# Revit family: H3006-TR035-EB
name_source: partatom
category: Aparatos sanitarios
units: mm (PartAtom-declared; Revit-internal decimal feet)

## family parameters
Anfitrión = Cara
Compartido = Sí
Corte con vacíos al cargar = No
Cota de conector redondo = Diámetro de uso
Número OmniClass = 23.45.05.14.17
Punto de cálculo de habitación = Sí
Tipo de pieza = Normal
Título OmniClass = Showers

## types (3) — shared parameters
Conexión = ½"-14 NPSM
Elevación por defecto = 0.5 "
Fabricante = HELVEX S.A. DE C.V.
Imagen de tipo = <Ninguno>
Presión máxima de trabajo = 85.3 psi
Presión mínima de trabajo = 14.2 psi

## per-type parameters (varying)
| type | Comentarios de tipo | Descripción | Material | Material EC | Modelo | Total Diameter | Total Length | URL |
| H3005-TR035 | Regadera redonda de plato ancho, multichorro 10"
3 Chorros.
3 Chorros. | Regadera redonda de plato ancho, multichorro 10"
3 Chorros.
3 Chorros. | 192_192_192 | <Por categoría> | H3005-TR035-EB | 9.6 " | 22.2 " |  |
| H3005-TR035-EB | Regadera de media y alta presión
3 Chorros.
3 Chorros. | Regadera de media y alta presión
3 Chorros.
3 Chorros. | Ébano | Ébano - Cromo | H3005-TR035 | 9.6 " | 22.2 " | https://www.helvex.com.mx |
| H3006-TR035-EB | Plato Ancho de 6" Regadera con brazo y chapetón.
3 Chorros. | Plato Ancho de 6" Regadera con brazo y chapetón.orros.
3 Chorros. | Ébano | Ébano - Cromo | H3006-TR035 | 6 " | 2.7 " | https://www.helvex.com.mx |

## geometry (parser evidence)
native form markers: Sweep x7
no freeform markers — native parametric forms only
